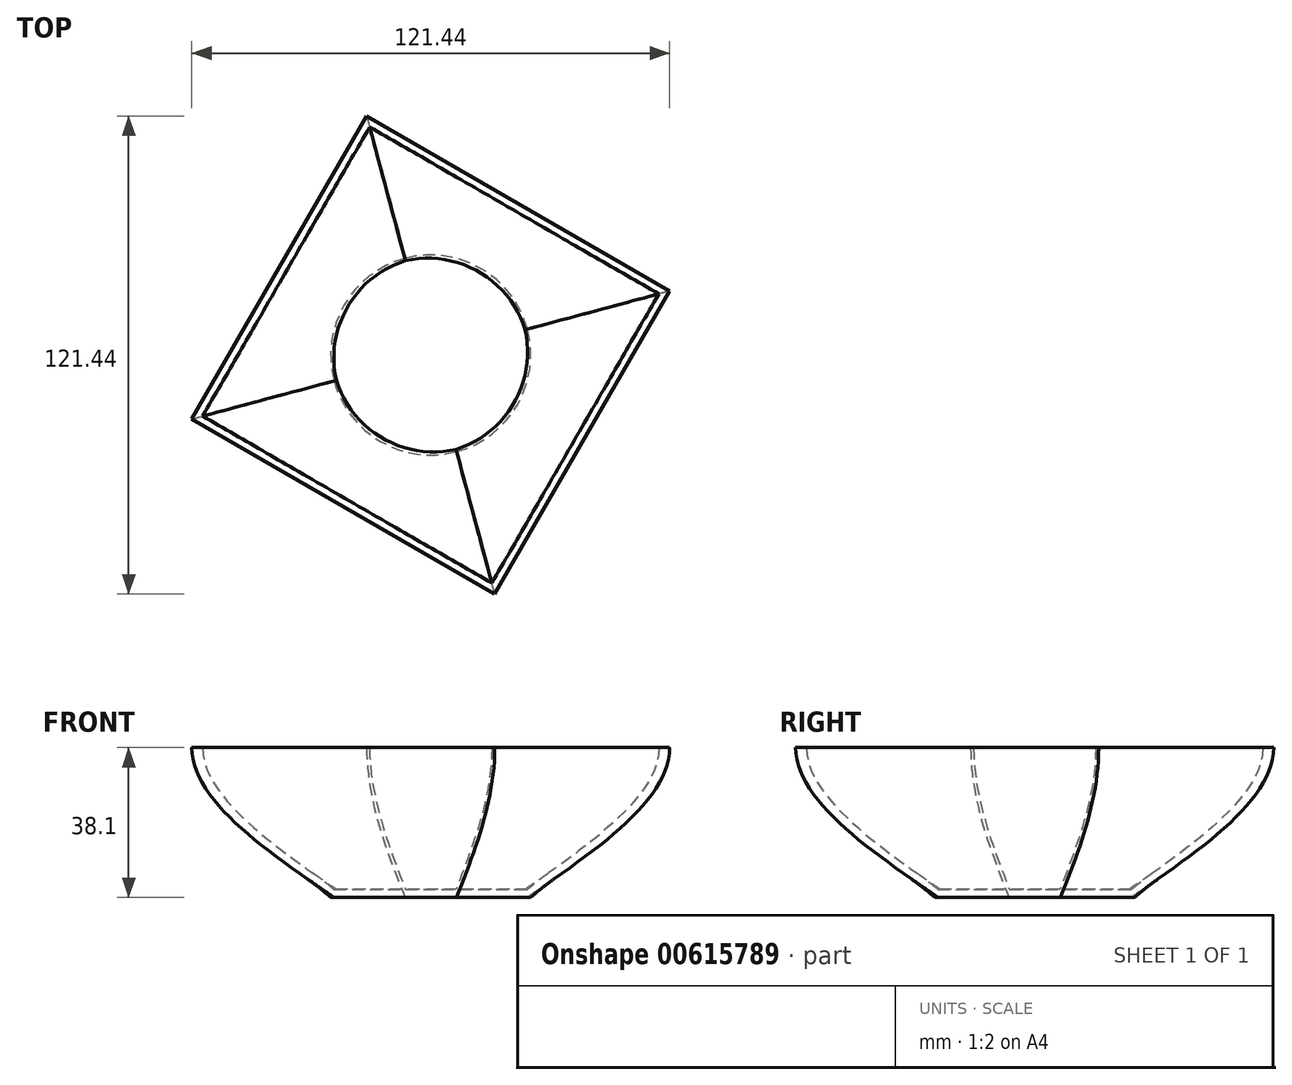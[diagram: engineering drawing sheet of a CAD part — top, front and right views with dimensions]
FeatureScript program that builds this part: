
annotation { "Feature Type Name" : "Feature", "Feature Type Description" : "" }
export const myFeature = defineFeature(function(context is Context, id is Id, definition is map)
    precondition{}
    {
        {
            var Q0;
            Q0=qCreatedBy(makeId("Top.planeOp"),FACE);
            var sketch = newSketch(context, id + "F0", { "sketchPlane" : qUnion([Q0])});
            skCircle(sketch, "E0", {"center": v(0, 0) * mm, "radius": 25.4 * mm});
            skSolve(sketch);
        }
        {
            var Q0;
            Q0=qCreatedBy(makeId("Top.planeOp"),FACE);
            cPlane(context, id + "F1", {"entities" : qUnion([Q0]), "cplaneType" : CPlaneType.OFFSET, "offset" : 38.1 * mm, "width" : 152.4 * mm, "height" : 152.4 * mm});
        }
        {
            var Q0;
            Q0=qCreatedBy(id+"F1.planeOp",FACE);
            var sketch = newSketch(context, id + "F2", { "sketchPlane" : qUnion([Q0])});
            skLineSegment(sketch, "E1.bottom", {"start": v(16.27, -60.72) * mm, "end": v(-60.72, -16.27) * mm});
            skLineSegment(sketch, "E1.top", {"start": v(60.72, 16.27) * mm, "end": v(-16.27, 60.72) * mm});
            skLineSegment(sketch, "E1.left", {"start": v(16.27, -60.72) * mm, "end": v(60.72, 16.27) * mm});
            skLineSegment(sketch, "E1.right", {"start": v(-60.72, -16.27) * mm, "end": v(-16.27, 60.72) * mm});
            skPoint(sketch, "E1.middle", {"position": v(0, 0) * mm});
            skSolve(sketch);
        }
        {
            var Q0;
            Q0=makeQuery(id+"F2.imprint","IMPRINT",FACE,{"disambiguationData":[TD([[makeQuery(id+"F2.imprint","IMPRINT",EDGE,{"derivedFrom":sQuery(id+"F2.wireOp",EDGE,"E1.bottom")}),-1.0]])]});
            var Q1;
            Q1=makeQuery(id+"F0.imprint","IMPRINT",FACE,{"disambiguationData":[TD([[makeQuery(id+"F0.imprint","IMPRINT",EDGE,{"derivedFrom":sQuery(id+"F0.wireOp",EDGE,"E0")}),1.0]])]});
            loft(context, id + "F3", {"startCondition" : LoftEndDerivativeType.NORMAL_TO_PROFILE, "startMagnitude" : 1, "sheetProfilesArray" : [{ "sheetProfileEntities" : qUnion([Q0]) }, { "sheetProfileEntities" : qUnion([Q1]) }]});
        }
        {
            var Q0;
            Q0=makeQuery(id+"F3.opLoft","CAP_FACE",FACE,{"disambiguationData":[OSD([makeQuery(id+"F2.imprint","IMPRINT",FACE,{"disambiguationData":[TD([[makeQuery(id+"F2.imprint","IMPRINT",EDGE,{"derivedFrom":sQuery(id+"F2.wireOp",EDGE,"E1.bottom")}),-1.0]])]})])],"isStart":true});
            shell(context, id + "F4", {"entities" : qUnion([Q0]), "thickness" : 2.03 * mm});
        }
    });
